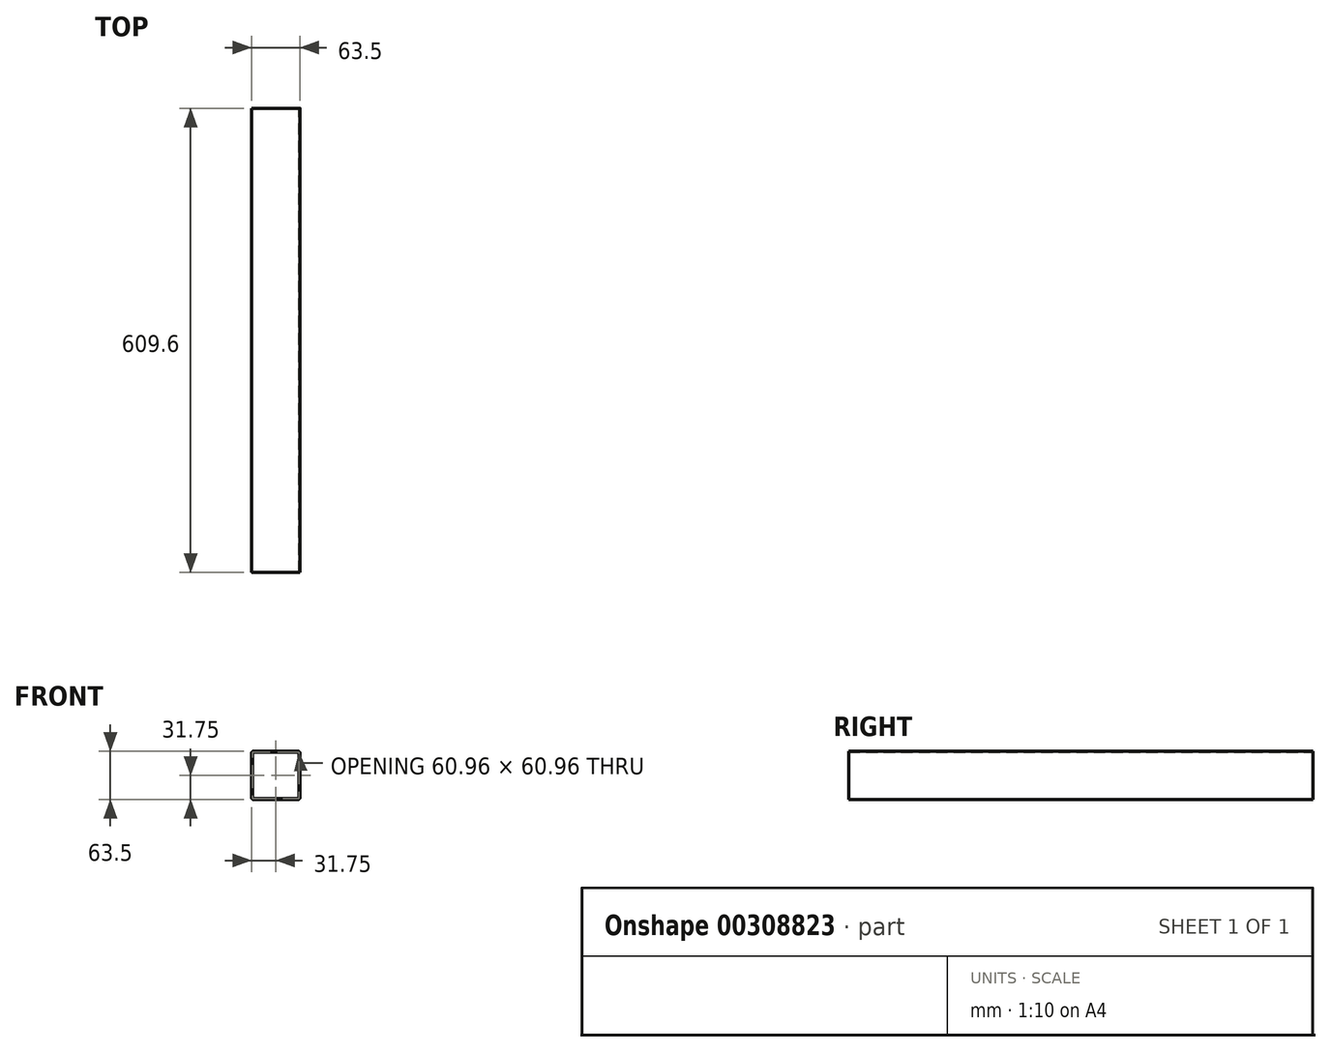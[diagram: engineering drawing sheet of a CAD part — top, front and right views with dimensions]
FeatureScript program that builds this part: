
annotation { "Feature Type Name" : "Feature", "Feature Type Description" : "" }
export const myFeature = defineFeature(function(context is Context, id is Id, definition is map)
    precondition{}
    {
        {
            var Q0;
            Q0=qCreatedBy(makeId("Front.planeOp"),FACE);
            var sketch = newSketch(context, id + "F0", { "sketchPlane" : qUnion([Q0])});
            skLineSegment(sketch, "E0.bottom", {"start": v(29.21, 31.75) * mm, "end": v(-29.21, 31.75) * mm});
            skLineSegment(sketch, "E0.top", {"start": v(29.2, -31.75) * mm, "end": v(-29.21, -31.75) * mm});
            skLineSegment(sketch, "E0.left", {"start": v(31.75, 29.21) * mm, "end": v(31.75, -29.21) * mm});
            skLineSegment(sketch, "E0.right", {"start": v(-31.75, 29.21) * mm, "end": v(-31.75, -29.21) * mm});
            skPoint(sketch, "E0.middle", {"position": v(0, 0) * mm});
            skLineSegment(sketch, "E1.bottom", {"start": v(27.94, 30.48) * mm, "end": v(-27.94, 30.48) * mm});
            skLineSegment(sketch, "E1.top", {"start": v(27.94, -30.48) * mm, "end": v(-27.94, -30.48) * mm});
            skLineSegment(sketch, "E1.left", {"start": v(30.48, 27.94) * mm, "end": v(30.48, -27.94) * mm});
            skLineSegment(sketch, "E1.right", {"start": v(-30.48, 27.94) * mm, "end": v(-30.48, -27.94) * mm});
            skPoint(sketch, "E2.visualSharp", {"position": v(-30.48, 30.48) * mm});
            skArc(sketch, "E2.filletArc", {"start": v(-27.94, 30.48) * mm, "mid": v(-29.74, 29.74) * mm, "end": v(-30.48, 27.94) * mm});
            skPoint(sketch, "E3.visualSharp", {"position": v(30.48, 30.48) * mm});
            skArc(sketch, "E3.filletArc", {"start": v(30.48, 27.94) * mm, "mid": v(29.74, 29.74) * mm, "end": v(27.94, 30.48) * mm});
            skPoint(sketch, "E4.visualSharp", {"position": v(31.75, 31.75) * mm});
            skArc(sketch, "E4.filletArc", {"start": v(31.75, 29.21) * mm, "mid": v(31, 31) * mm, "end": v(29.21, 31.75) * mm});
            skPoint(sketch, "E5.visualSharp", {"position": v(30.48, -30.48) * mm});
            skArc(sketch, "E5.filletArc", {"start": v(27.94, -30.48) * mm, "mid": v(29.74, -29.74) * mm, "end": v(30.48, -27.94) * mm});
            skPoint(sketch, "E6.visualSharp", {"position": v(31.75, -31.75) * mm});
            skArc(sketch, "E6.filletArc", {"start": v(29.2, -31.75) * mm, "mid": v(31, -31) * mm, "end": v(31.75, -29.21) * mm});
            skPoint(sketch, "E7.visualSharp", {"position": v(-30.48, -30.48) * mm});
            skArc(sketch, "E7.filletArc", {"start": v(-30.48, -27.94) * mm, "mid": v(-29.74, -29.74) * mm, "end": v(-27.94, -30.48) * mm});
            skPoint(sketch, "E8.visualSharp", {"position": v(-31.75, -31.75) * mm});
            skArc(sketch, "E8.filletArc", {"start": v(-31.75, -29.21) * mm, "mid": v(-31, -31) * mm, "end": v(-29.21, -31.75) * mm});
            skPoint(sketch, "E9.visualSharp", {"position": v(-31.75, 31.75) * mm});
            skArc(sketch, "E9.filletArc", {"start": v(-29.21, 31.75) * mm, "mid": v(-31, 31) * mm, "end": v(-31.75, 29.21) * mm});
            skSolve(sketch);
        }
        {
            var Q0;
            Q0 = qSketchRegion(id + "F0", true);
            extrude(context, id + "F1", {"entities" : qUnion([Q0]), "depth" : 609.6 * mm});
        }
    });
